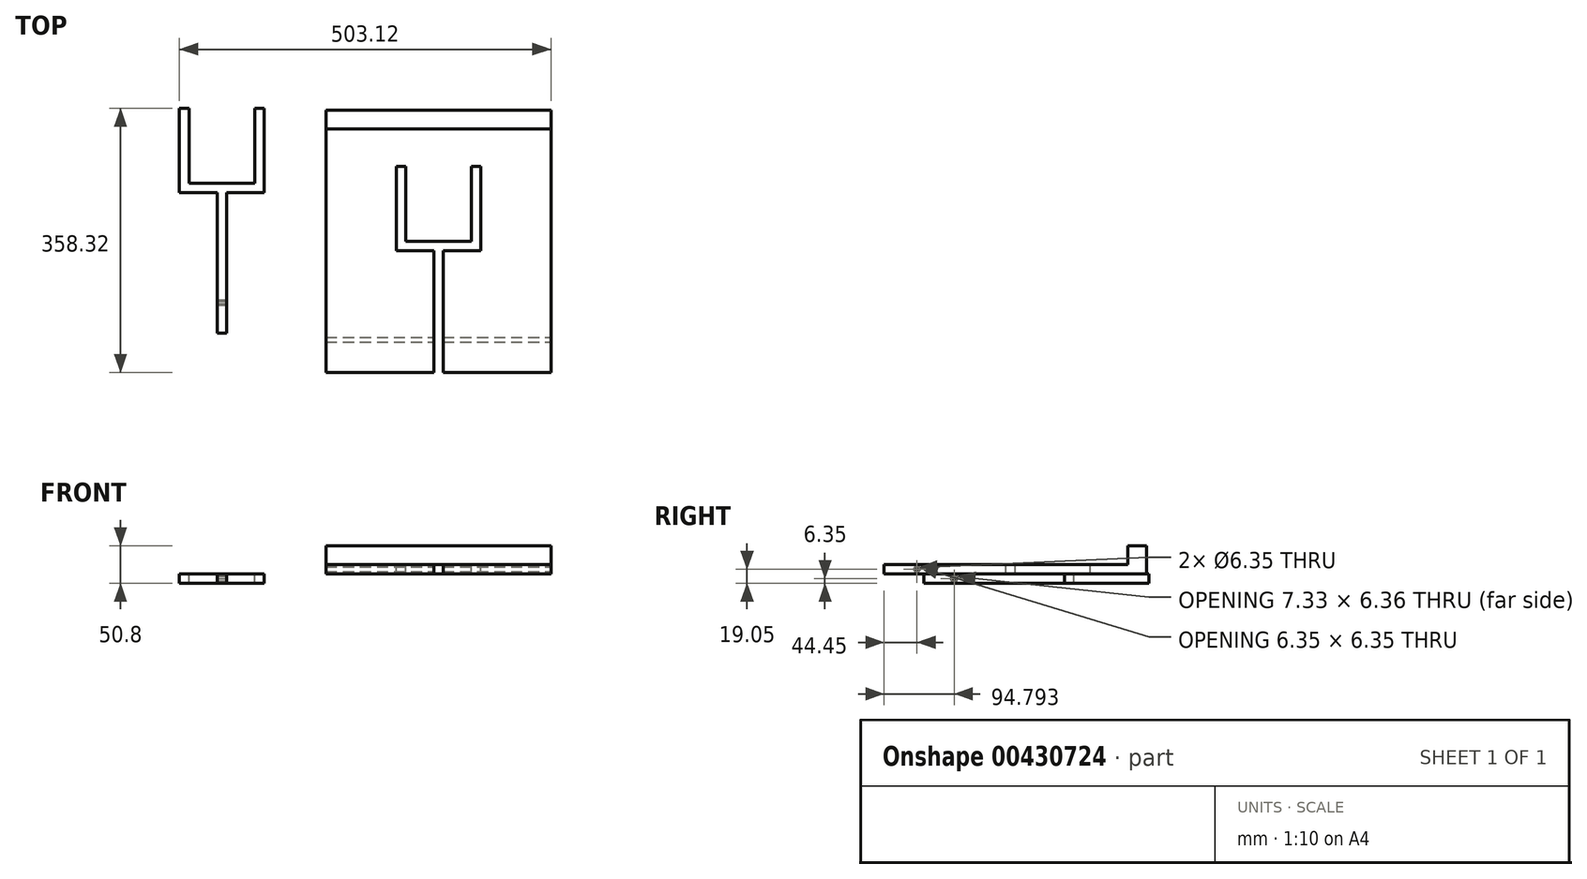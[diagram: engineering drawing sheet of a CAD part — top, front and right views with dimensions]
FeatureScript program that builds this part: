
annotation { "Feature Type Name" : "Feature", "Feature Type Description" : "" }
export const myFeature = defineFeature(function(context is Context, id is Id, definition is map)
    precondition{}
    {
        {
            var Q0;
            Q0=qCreatedBy(makeId("Top.planeOp"),FACE);
            var sketch = newSketch(context, id + "F0", { "sketchPlane" : qUnion([Q0])});
            skLineSegment(sketch, "E0.bottom", {"start": v(-152.4, -177.8) * mm, "end": v(152.4, -177.8) * mm});
            skLineSegment(sketch, "E0.top", {"start": v(-152.4, 177.8) * mm, "end": v(152.4, 177.8) * mm});
            skLineSegment(sketch, "E0.left", {"start": v(-152.4, -177.8) * mm, "end": v(-152.4, 177.8) * mm});
            skLineSegment(sketch, "E0.right", {"start": v(152.4, -177.8) * mm, "end": v(152.4, 177.8) * mm});
            skPoint(sketch, "E0.middle", {"position": v(0, 0) * mm});
            skLineSegment(sketch, "E1.top", {"start": v(-152.4, 152.4) * mm, "end": v(152.4, 152.4) * mm});
            skLineSegment(sketch, "E1.left", {"start": v(-152.4, 177.8) * mm, "end": v(-152.4, 152.4) * mm});
            skLineSegment(sketch, "E1.right", {"start": v(152.4, 177.8) * mm, "end": v(152.4, 152.4) * mm});
            skSolve(sketch);
        }
        {
            var Q0;
            Q0=makeQuery(id+"F0.imprint","IMPRINT",FACE,{"disambiguationData":[TD([[makeQuery(id+"F0.imprint","IMPRINT",EDGE,{"derivedFrom":sQuery(id+"F0.wireOp",EDGE,"E0.bottom")}),1.0]])]});
            extrude(context, id + "F1", {"entities" : qUnion([Q0]), "depth" : 12.7 * mm});
        }
        {
            var Q0;
            Q0=makeQuery(id+"F1.opExtrude","CAP_FACE",FACE,{"disambiguationData":[OSD([sQuery(id+"F0.wireOp",EDGE,"E0.bottom"),sQuery(id+"F0.wireOp",EDGE,"E0.top"),sQuery(id+"F0.wireOp",EDGE,"E0.left"),sQuery(id+"F0.wireOp",EDGE,"E0.right")])],"isStart":false});
            var sketch = newSketch(context, id + "F2", { "sketchPlane" : qUnion([Q0])});
            skLineSegment(sketch, "E2.bottom", {"start": v(6.35, -177.8) * mm, "end": v(-6.35, -177.8) * mm});
            skLineSegment(sketch, "E2.top", {"start": v(6.35, 0) * mm, "end": v(-6.35, 0) * mm});
            skLineSegment(sketch, "E2.left", {"start": v(6.35, -177.8) * mm, "end": v(6.35, 0) * mm});
            skLineSegment(sketch, "E2.right", {"start": v(-6.35, -177.8) * mm, "end": v(-6.35, 0) * mm});
            skPoint(sketch, "E2.middle", {"position": v(0, -88.9) * mm});
            skLineSegment(sketch, "E3.bottom", {"start": v(-6.35, 0) * mm, "end": v(-57.15, 0) * mm});
            skLineSegment(sketch, "E3.top", {"start": v(-6.35, -12.7) * mm, "end": v(-57.15, -12.7) * mm});
            skLineSegment(sketch, "E3.left", {"start": v(-6.35, 0) * mm, "end": v(-6.35, -12.7) * mm});
            skLineSegment(sketch, "E3.right", {"start": v(-57.15, 0) * mm, "end": v(-57.15, -12.7) * mm});
            skLineSegment(sketch, "E4.bottom", {"start": v(6.35, 0) * mm, "end": v(57.15, 0) * mm});
            skLineSegment(sketch, "E4.top", {"start": v(6.35, -12.7) * mm, "end": v(57.15, -12.7) * mm});
            skLineSegment(sketch, "E4.left", {"start": v(6.35, 0) * mm, "end": v(6.35, -12.7) * mm});
            skLineSegment(sketch, "E4.right", {"start": v(57.15, 0) * mm, "end": v(57.15, -12.7) * mm});
            skLineSegment(sketch, "E5.bottom", {"start": v(-57.15, 0) * mm, "end": v(-44.45, 0) * mm});
            skLineSegment(sketch, "E5.top", {"start": v(-57.15, 101.6) * mm, "end": v(-44.45, 101.6) * mm});
            skLineSegment(sketch, "E5.left", {"start": v(-57.15, 0) * mm, "end": v(-57.15, 101.6) * mm});
            skLineSegment(sketch, "E5.right", {"start": v(-44.45, 0) * mm, "end": v(-44.45, 101.6) * mm});
            skLineSegment(sketch, "E6.bottom", {"start": v(57.15, 0) * mm, "end": v(44.45, 0) * mm});
            skLineSegment(sketch, "E6.top", {"start": v(57.15, 101.6) * mm, "end": v(44.45, 101.6) * mm});
            skLineSegment(sketch, "E6.left", {"start": v(57.15, 0) * mm, "end": v(57.15, 101.6) * mm});
            skLineSegment(sketch, "E6.right", {"start": v(44.45, 0) * mm, "end": v(44.45, 101.6) * mm});
            skSolve(sketch);
        }
        {
            var Q0;
            Q0 = qSketchRegion(id + "F2", true);
            extrude(context, id + "F3", {"entities" : qUnion([Q0]), "operationType" : NewBodyOperationType.REMOVE, "oppositeDirection" : true, "depth" : 25.4 * mm});
        }
        {
            var Q0;
            Q0=makeQuery(id+"F3.boolean.opBoolean","COPY",FACE,{"derivedFrom":makeQuery(id+"F3.opExtrude","SWEPT_FACE",FACE,{"disambiguationData":[OSD([sQuery(id+"F2.wireOp",EDGE,"E2.right")])]})});
            var sketch = newSketch(context, id + "F4", { "sketchPlane" : qUnion([Q0])});
            skLineSegment(sketch, "E7", {"start": v(-177.8, 12.7) * mm, "end": v(-133.35, 12.7) * mm});
            skLineSegment(sketch, "E8", {"start": v(-133.35, 12.7) * mm, "end": v(-133.35, 0) * mm});
            skPoint(sketch, "E9", {"position": v(-133.35, 6.35) * mm});
            skCircle(sketch, "E10", {"center": v(-133.35, 6.35) * mm, "radius": 3.18 * mm});
            skSolve(sketch);
        }
        {
            var Q0;
            Q0 = qSketchRegion(id + "F4", true);
            extrude(context, id + "F5", {"entities" : qUnion([Q0]), "operationType" : NewBodyOperationType.REMOVE, "oppositeDirection" : true, "depth" : 203.2 * mm, "hasSecondDirection" : true, "secondDirectionOppositeDirection" : false, "secondDirectionDepth" : 203.2 * mm});
        }
        {
            var Q0;
            Q0=qCreatedBy(makeId("Top.planeOp"),FACE);
            var sketch = newSketch(context, id + "F6", { "sketchPlane" : qUnion([Q0])});
            skLineSegment(sketch, "E11", {"start": v(-299.92, -124.28) * mm, "end": v(-299.92, 66.22) * mm});
            skLineSegment(sketch, "E12", {"start": v(-299.92, 66.22) * mm, "end": v(-350.72, 66.22) * mm});
            skLineSegment(sketch, "E13", {"start": v(-350.72, 66.22) * mm, "end": v(-350.72, 180.52) * mm});
            skLineSegment(sketch, "E14", {"start": v(-350.72, 180.52) * mm, "end": v(-338.02, 180.52) * mm});
            skLineSegment(sketch, "E15", {"start": v(-338.02, 180.52) * mm, "end": v(-338.02, 78.92) * mm});
            skLineSegment(sketch, "E16", {"start": v(-338.02, 78.92) * mm, "end": v(-249.12, 78.92) * mm});
            skLineSegment(sketch, "E17", {"start": v(-249.12, 78.92) * mm, "end": v(-249.12, 180.52) * mm});
            skLineSegment(sketch, "E18", {"start": v(-249.12, 180.52) * mm, "end": v(-236.42, 180.52) * mm});
            skLineSegment(sketch, "E19", {"start": v(-236.42, 180.52) * mm, "end": v(-236.42, 66.22) * mm});
            skLineSegment(sketch, "E20", {"start": v(-236.42, 66.22) * mm, "end": v(-287.22, 66.22) * mm});
            skLineSegment(sketch, "E21", {"start": v(-287.22, 66.22) * mm, "end": v(-287.22, -124.28) * mm});
            skLineSegment(sketch, "E22", {"start": v(-287.22, -124.28) * mm, "end": v(-299.92, -124.28) * mm});
            skPoint(sketch, "E23", {"position": v(-287.22, -83) * mm});
            skSolve(sketch);
        }
        {
            var Q0;
            Q0=makeQuery(id+"F6.imprint","IMPRINT",FACE,{"disambiguationData":[TD([[makeQuery(id+"F6.imprint","IMPRINT",EDGE,{"derivedFrom":sQuery(id+"F6.wireOp",EDGE,"E11")}),-1.0]])]});
            extrude(context, id + "F7", {"entities" : qUnion([Q0]), "oppositeDirection" : true, "depth" : 12.7 * mm});
        }
        {
            var Q0;
            Q0=makeQuery(id+"F7.opExtrude","SWEPT_FACE",FACE,{"disambiguationData":[OSD([sQuery(id+"F6.wireOp",EDGE,"E21")])]});
            var sketch = newSketch(context, id + "F8", { "sketchPlane" : qUnion([Q0])});
            skCircle(sketch, "E24.cCircle", {"center": v(-83, -6.35) * mm, "radius": 3.18 * mm, "construction": true});
            skLineSegment(sketch, "E24.0", {"start": v(-84.83, -9.53) * mm, "end": v(-86.67, -6.36) * mm});
            skLineSegment(sketch, "E24.1", {"start": v(-86.67, -6.36) * mm, "end": v(-84.85, -3.18) * mm});
            skLineSegment(sketch, "E24.2", {"start": v(-84.85, -3.18) * mm, "end": v(-81.19, -3.17) * mm});
            skLineSegment(sketch, "E24.3", {"start": v(-81.19, -3.17) * mm, "end": v(-79.34, -6.34) * mm});
            skLineSegment(sketch, "E24.4", {"start": v(-79.34, -6.34) * mm, "end": v(-81.16, -9.52) * mm});
            skLineSegment(sketch, "E24.5", {"start": v(-81.16, -9.52) * mm, "end": v(-84.83, -9.53) * mm});
            skPoint(sketch, "E24.0.midPoint", {"position": v(-85.75, -7.95) * mm});
            skSolve(sketch);
        }
        {
            var Q0;
            Q0=makeQuery(id+"F8.imprint","IMPRINT",FACE,{"disambiguationData":[TD([[makeQuery(id+"F8.imprint","IMPRINT",EDGE,{"derivedFrom":sQuery(id+"F8.wireOp",EDGE,"E24.0")}),-1.0]])]});
            extrude(context, id + "F9", {"entities" : qUnion([Q0]), "operationType" : NewBodyOperationType.REMOVE, "oppositeDirection" : true, "depth" : 12.7 * mm});
        }
        {
            var Q0;
            Q0=makeQuery(id+"F0.imprint","IMPRINT",FACE,{"disambiguationData":[TD([[makeQuery(id+"F0.imprint","IMPRINT",EDGE,{"derivedFrom":sQuery(id+"F0.wireOp",EDGE,"E0.top")}),-1.0]])]});
            extrude(context, id + "F10", {"entities" : qUnion([Q0]), "operationType" : NewBodyOperationType.ADD, "depth" : 38.1 * mm});
        }
    });
